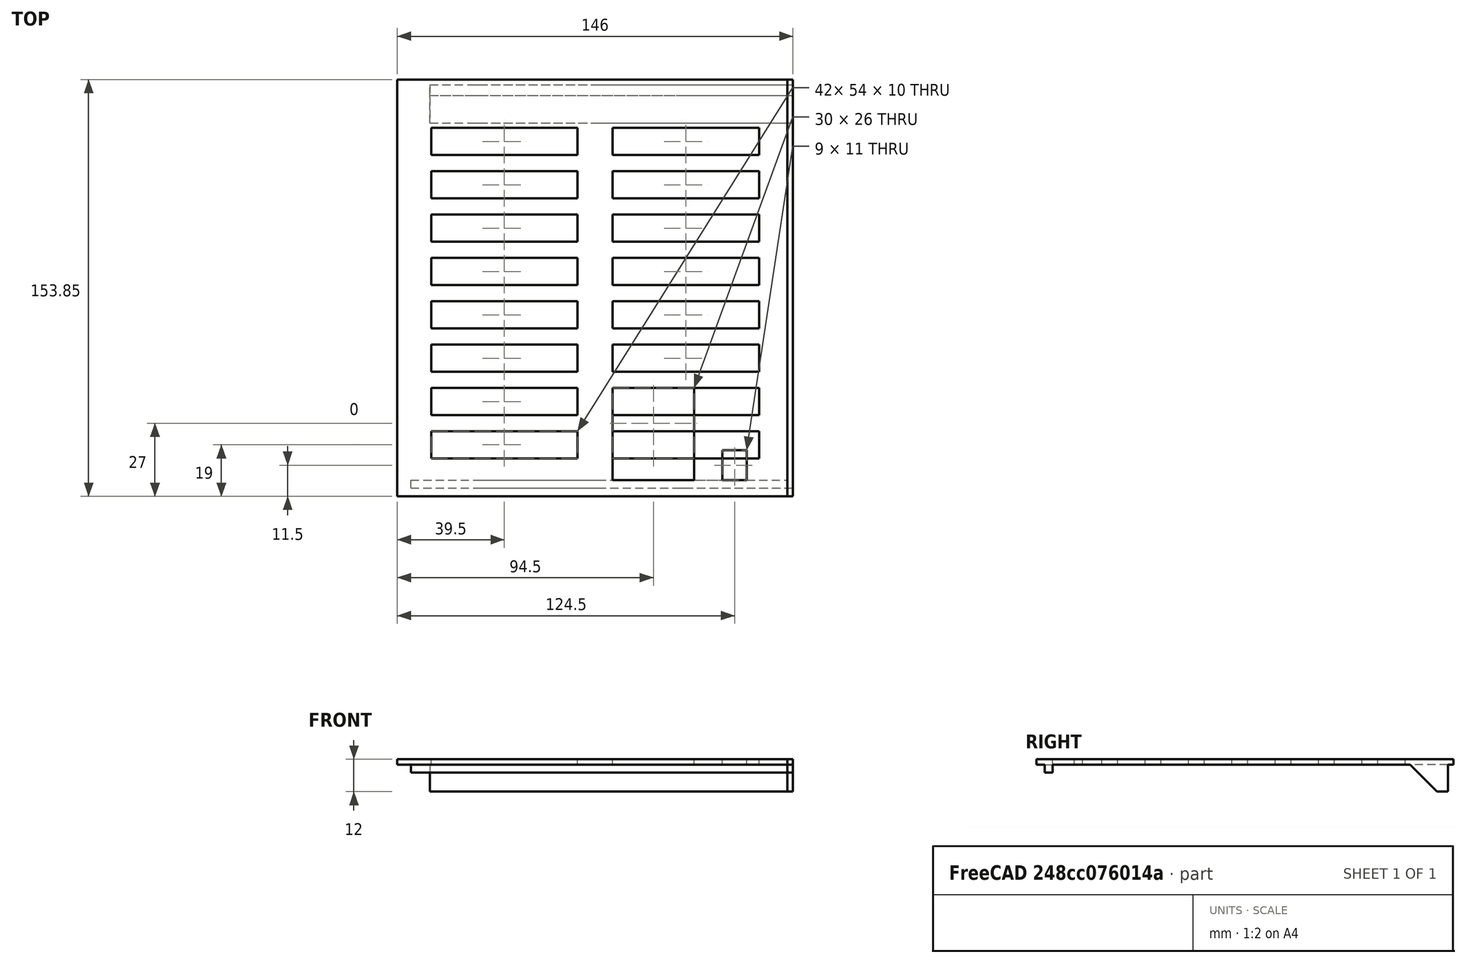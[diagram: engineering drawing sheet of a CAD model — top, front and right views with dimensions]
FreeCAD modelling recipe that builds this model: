
FCSTD DOCUMENT  (FreeCAD 0.17R13522 (Git))
Label: lateral_derecho_v3
License: CreativeCommons Attribution-ShareAlike
LicenseURL: http://creativecommons.org/licenses/by-sa/4.0/
objects: Part::Box×10, Part::Cut×8, Part::Feature×6, Part::MultiFuse×4, Part::FeaturePython×1
note: 29 computed .brp shape members not serialized (recipe doc carries the construction recipe); baked Part::Feature solids carry a one-line shape summary decoded from their .brp

FEATURE [Part::Feature] Cut003001  label="Cut004"
  shape: bbox 30 x 153.9 x 12 mm, 47 faces (baked)
FEATURE [Part::Feature] Cut004001  label="Cut005"
  shape: bbox 108 x 153.9 x 12 mm, 79 faces (baked)
FEATURE [Part::Feature] Cut004002  label="Cut006"
  shape: bbox 72 x 153.9 x 12 mm, 47 faces (baked)
FEATURE [Part::Box] Box  label="Cube"
  AttacherType = Attacher::AttachEngine3D
  Height = 30
  Length = 30
  Placement = pos=(30,-16,-18) rot=(0,0,1;0rad)
  Width = 200
FEATURE [Part::Cut] Cut
  Base = -> Cut004001
  Placement = pos=(-30,0,0) rot=(0,0,1;0rad)
  Tool = -> Box
FEATURE [Part::Box] Box001  label="Cube001"
  AttacherType = Attacher::AttachEngine3D
  Height = 20
  Length = 1
  Placement = pos=(67.5,14,-10) rot=(0,0,1;0rad)
  Width = 10
FEATURE [Part::FeaturePython] Array  # Draft array (typed FeaturePython)
  Angle = 360
  ArrayType = 0
  Axis = (0,0,1)
  Base = -> Box001
  Center = (0,0,0)
  Fuse = false
  IntervalAxis = (0,0,0)
  IntervalX = (14,0,0)
  IntervalY = (0,16,0)
  IntervalZ = (0,0,0)
  NumberPolar = 1
  NumberX = 2
  NumberY = 8
  NumberZ = 1
FEATURE [Part::Cut] Cut004003
  Base = -> Cut
  Placement = pos=(-2,0,0) rot=(0,0,1;0rad)
  Tool = -> Array
FEATURE [Part::Box] Box002  label="Cube002"
  AttacherType = Attacher::AttachEngine3D
  Height = 31
  Length = 30
  Placement = pos=(138,-15,0) rot=(0,0,1;0rad)
  Width = 200
FEATURE [Part::Cut] Cut004004
  Base = -> Cut004002
  Placement = pos=(-64,0,0) rot=(0,0,1;0rad)
  Tool = -> Box002
FEATURE [Part::MultiFuse] Fusion
  Shapes = -> [Cut003001,Cut004003]
FEATURE [Part::MultiFuse] Fusion001
  Shapes = -> [Fusion,Cut004004]
FEATURE [Part::Feature] Fusion001001  label="Fusion002"
  shape: bbox 146 x 153.9 x 12 mm, 79 faces (baked)
FEATURE [Part::Box] Box003  label="Cube003"
  AttacherType = Attacher::AttachEngine3D
  Height = 22
  Length = 10
  Placement = pos=(144,-16,-12) rot=(0,0,1;0rad)
  Width = 200
FEATURE [Part::Cut] Cut004005
  Base = -> Fusion001001
  Tool = -> Box003
FEATURE [Part::Box] Box004  label="Cube004"
  AttacherType = Attacher::AttachEngine3D
  Height = 10
  Length = 30
  Placement = pos=(79.5,6,-3) rot=(0,0,1;0rad)
  Width = 33
FEATURE [Part::Cut] Cut004006
  Base = -> Cut004005
  Tool = -> Box004
FEATURE [Part::Box] Box005  label="Cube005"
  AttacherType = Attacher::AttachEngine3D
  Height = 2
  Length = 25
  Placement = pos=(109.5,13,0) rot=(0,0,1;0rad)
  Width = 29
FEATURE [Part::MultiFuse] Fusion001002
  Shapes = -> [Box005,Cut004006]
FEATURE [Part::Box] Box006  label="Cube006"
  AttacherType = Attacher::AttachEngine3D
  Height = 20
  Length = 9
  Placement = pos=(120,6,-8) rot=(0,0,1;0rad)
  Width = 11
FEATURE [Part::Feature] Fusion001002001  label="Fusion001003"
  shape: bbox 144 x 153.9 x 12 mm, 75 faces (baked)
FEATURE [Part::Box] Box007  label="Cube007"
  AttacherType = Attacher::AttachEngine3D
  Height = 10
  Length = 30
  Placement = pos=(79.5,6,-3) rot=(0,0,1;0rad)
  Width = 33
FEATURE [Part::Cut] Cut004007
  Base = -> Fusion001002001
  Tool = -> Box006
FEATURE [Part::Cut] Cut004008
  Base = -> Cut004005
  Tool = -> Box007
FEATURE [Part::Box] Box008  label="Cube008"
  AttacherType = Attacher::AttachEngine3D
  Height = 2
  Length = 25
  Placement = pos=(109.5,13,0) rot=(0,0,1;0rad)
  Width = 29
FEATURE [Part::MultiFuse] Fusion001002002
  Shapes = -> [Cut004008,Box008]
FEATURE [Part::Feature] Fusion001002002001  label="Fusion001002003"
  shape: bbox 144 x 153.9 x 12 mm, 74 faces (baked)
FEATURE [Part::Box] Box009  label="Cube009"
  AttacherType = Attacher::AttachEngine3D
  Height = 20
  Length = 9
  Placement = pos=(120,6,-8) rot=(0,0,1;0rad)
  Width = 11
FEATURE [Part::Cut] Cut004009
  Base = -> Fusion001002002001
  Tool = -> Box009
